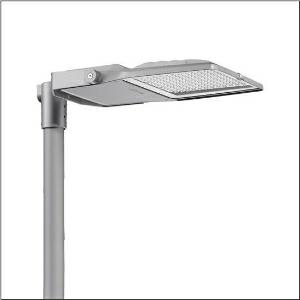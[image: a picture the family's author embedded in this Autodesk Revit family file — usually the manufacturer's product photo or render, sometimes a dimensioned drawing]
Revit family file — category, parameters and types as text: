
# Revit family: floodlight_fl_21_midi___pl61_5xa7786f2c3a_551f
name_source: partatom
category: Lighting Fixtures
units: mm (PartAtom-declared; Revit-internal decimal feet)

## family parameters
Cut with Voids When Loaded = No
Host = Face
Light Source = No
Part Type = Normal
Room Calculation Point = No
Round Connector Dimension = Use Diameter
Shared = No

## types (1)
- --- (1 x LED, 35100 lm, 271.6 W, 3000K)
    Apparent Load = 272 VA
    CIE Flux Codes = 33 65 98 100 100
    Color Rendering = 70
    Color Temperature = 3000K
    Default Elevation = 1800 mm
    Description = Floodlight FL 21 midi, floodlight, primary light control with lens, of PMMA, primary optical cover: protective disc, of toughened safety glass, transparent, light distribution: PL61, light emission: direct distribution, installation type: surface-mounted, LED, High Power LED, rated luminous flux: 35.100lm, luminous efficacy: 129lm/W, light colour: 730, colour temperature: 3000K, control gear: Smart Interface (Zhaga), control: flexible luminous flux parameterisation, time-dependent luminous flux control, constant luminous flux control, overheat protection, pre-setting: logarithmic dimming characteristic, with terminal, 6-pole, mains connection: 220..240V, AC, 50/60Hz, start of lifetime: 272W, end of service life: 287W, reduction: 123W, luminaire housing, of diecast aluminium, powder-coated, Siteco® metallic grey (DB 702S), corrosivity category C5 mid according to DIN EN ISO 12944, suitable for swimming pools, chlorine-resistant, sealing non-destructively replaceable, please order mast flange separately, mast bracket, of steel, galvanised, powder-coated, Siteco® metallic grey (DB 702S), Smart Interface below and above, protection rating (complete): IP66, insulation class (complete): insulation class II (safety insulation), certification: CE, ENEC, VDE, protection symbol: D, impact resistance: IK08, permissible operating ambient temperature: -40..+40°C, permissible operating ambient temperature for outdoor applications: -40..+50°C, standard: DIN EN 12944, LABS conformity tested according to VDMA 24364:2018-05, packaging unit: 1 piece

Light Distribution: PL61
    Height = 76 mm
    Lamp = 1 x LED
    Lamp Light Flux = 35100 lm
    Lamp Power = 271.6 W
    Lamp count = 1
    Length = 657 mm
    Luminous efficacy = 129 lm/W
    Manufacturer = Siteco
    ModVariant = No
    Model = 5XA7786F2C3A
    Number of Poles = 1
    OnlyDefault = Yes
    Power Factor = 1
    Product Name = Floodlight FL 21 midi | PL61
    Product group = floodlight | pylon annexe
    ProductGroupID = 6201
    Protection Class = Protection class II
    Protection Degree = IP 66
    RLX_Detail_Level = 1
    RLX_Emergency_Light_Flux = 0 lm
    RLX_Emergency_Type = 0
    RLX_Emergency_Type_DB = No
    RlxData = <blob elided: 153629 chars, md5=dcecae5a>
    Socket = socket
    Standby Power = 0 W
    System Light Flux = 35100 lm
    System Power = 272 W
    Type Comments = factory setting: luminous flux: 100 % | dim-lin: 254 | 620 mA
    Type Image = l_1007123.jpg
    URL = http://relux.com
    VarID = @adj_215225
    Voltage = 0 V
    Weight = 0.00 kg
    Width = 442 mm

## geometry (parser evidence)
native form markers: Blend x4, Sweep x15
no freeform markers — native parametric forms only
